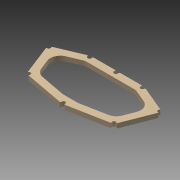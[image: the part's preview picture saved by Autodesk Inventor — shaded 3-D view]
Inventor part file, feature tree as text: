
AUTODESK INVENTOR PART (.ipt)
format: ipt  version: 2015 (Build 190159000, 159)  size: 195,072 bytes
history: native  units: mm
features: fillet x9, hole x5, extrude x2, sketch x2, mirror x1
ambient origin geometry x8: Origin, YZ Plane, XZ Plane, XY Plane, X Axis, Y Axis, Z Axis, Center Point
bodies: Solid4 (feature_tree)
feature tree (19):
  extrude  "Extrusion4"  Depth=228.6mm
  hole  "Hole2"  [1 undecoded]
  hole  "Hole3"  [1 undecoded]
  hole  "Hole4"  [1 undecoded]
  hole  "Hole5"  [1 undecoded]
  hole  "Hole6"  [1 undecoded]
  fillet  "Fillet6"  Radius=18.0mm
  fillet  "Fillet7"  Radius=4.0mm
  fillet  "Fillet8"  Radius=3.0mm
  fillet  "Fillet9"  Radius=3.0mm
  fillet  "Fillet10"  Radius=1.0mm
  fillet  "Fillet11"  Radius=1.0mm
  fillet  "Fillet12"  Radius=1.0mm
  fillet  "Fillet13"  Radius=1.0mm
  extrude  "Extrusion5"  Depth=3.0mm
  fillet  "Fillet14"  Radius=30.0mm
  mirror  "Mirror3"
  sketch  "Sketch1"  dims[d9=228.6mm d11=225.8568mm]
  sketch  "Sketch4"  dims[d15=178.0032mm d20=172.5168mm d22=41.148mm d39=105.7656mm d41=0.0mm d42=8.2296mm d98=18.0mm d99=0.0mm d159=10.0mm d160=10.0mm d102=15.0mm d103=6.0mm d104=3.023mm d105=2.0mm d106=14.3117mm d107=8.0mm d108=20.594885mm d161=10.0mm d162=10.0mm d111=15.0mm d112=6.0mm d113=3.023mm d114=2.0mm d115=14.3117mm d116=8.0mm d117=20.594885mm d163=10.0mm d164=10.0mm d124=15.0mm d125=6.0mm d126=3.023mm d127=2.0mm d128=14.3117mm d129=8.0mm d130=20.594885mm d165=10.0mm d166=10.0mm d133=15.0mm d134=6.0mm d135=3.023mm d136=2.0mm d137=14.3117mm d138=8.0mm d139=20.594885mm d167=10.0mm d168=10.0mm d150=15.0mm d151=6.0mm d152=4.0mm d153=2.0mm d154=90.0deg d155=8.0mm d156=20.594885mm d157=4.0mm d158=3.0mm d169=3.0mm d170=1.0mm d171=1.0mm d172=1.0mm d173=1.0mm d174=3.0mm d175=30.0mm d176=28.0mm d177=28.0mm d178=28.0mm d179=28.0mm d180=10.0mm d181=0.0mm d182=40.0mm]
note: 5 required parameter values undecoded (feature->parameter linkage not recoverable at this tier; creation-order binding heuristic only, values carry confidence <= 0.55)
